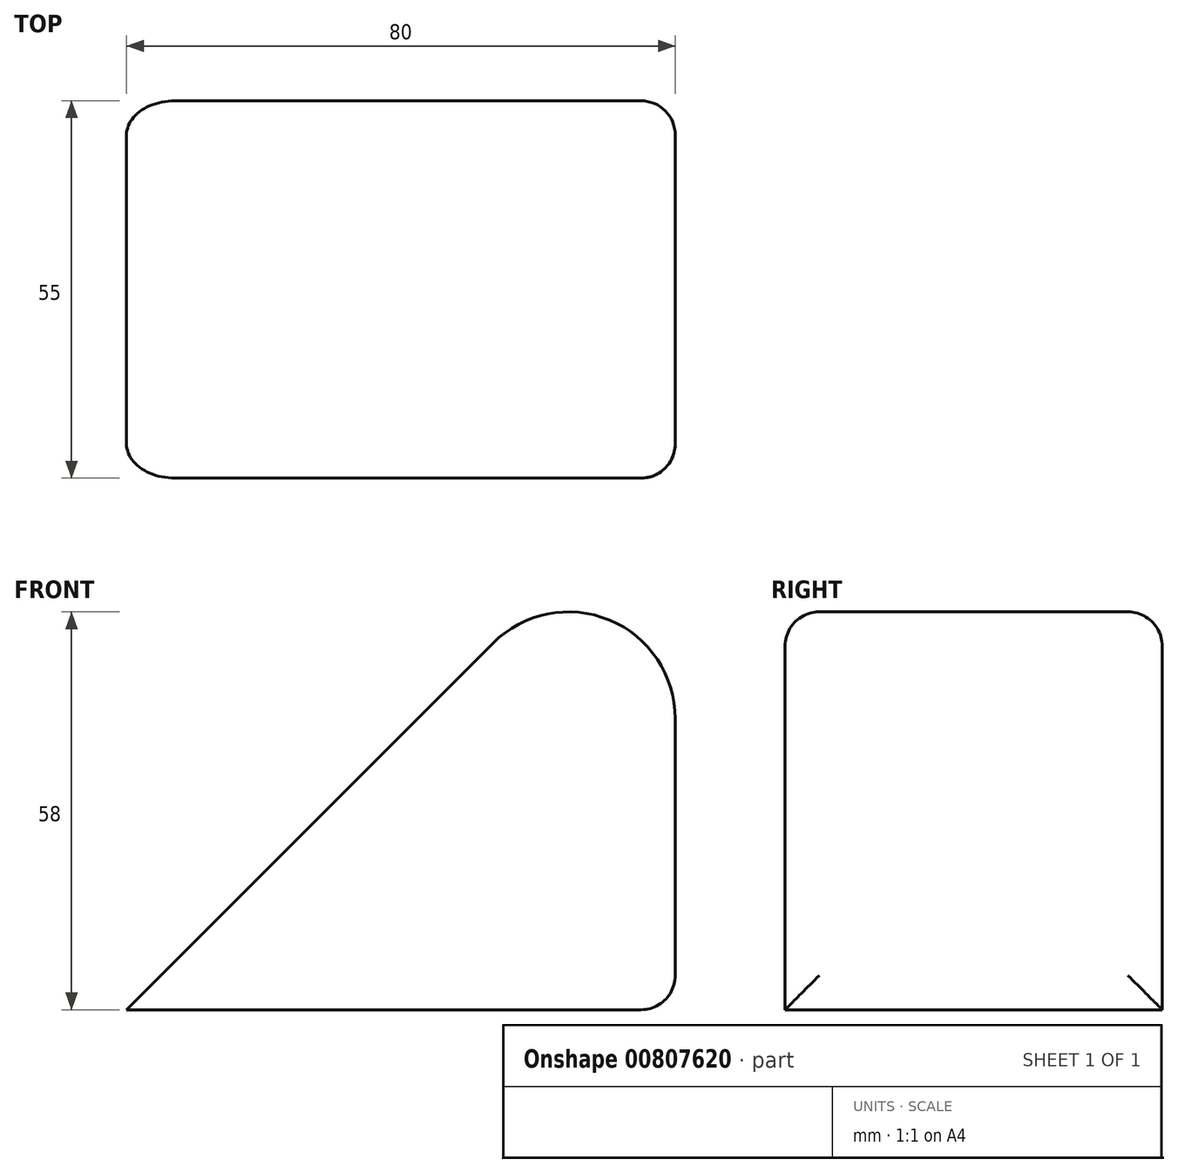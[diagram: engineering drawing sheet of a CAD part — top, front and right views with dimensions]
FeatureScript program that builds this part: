
annotation { "Feature Type Name" : "Feature", "Feature Type Description" : "" }
export const myFeature = defineFeature(function(context is Context, id is Id, definition is map)
    precondition{}
    {
        {
            var Q0;
            Q0=qCreatedBy(makeId("Front.planeOp"),FACE);
            var sketch = newSketch(context, id + "F0", { "sketchPlane" : qUnion([Q0])});
            skLineSegment(sketch, "E0", {"start": v(0, 0) * mm, "end": v(0, 80) * mm});
            skLineSegment(sketch, "E1", {"start": v(0, 80) * mm, "end": v(-80, 0) * mm});
            skLineSegment(sketch, "E2", {"start": v(-80, 0) * mm, "end": v(0, 0) * mm});
            skSolve(sketch);
        }
        {
            var Q0;
            Q0 = qSketchRegion(id + "F0", true);
            extrude(context, id + "F1", {"entities" : qUnion([Q0]), "depth" : 55 * mm, "offsetDistance" : 25 * mm});
        }
        {
            var Q0;
            Q0=makeQuery(id+"F1.opExtrude","SWEPT_EDGE",EDGE,{"disambiguationData":[OSD([sQuery(id+"F0.wireOp",EDGE,"E0"),sQuery(id+"F0.wireOp",EDGE,"E1")])]});
            fillet(context, id + "F2", {"entities" : qUnion([Q0]), "radius" : 15.56 * mm, "tangentPropagation" : true, "allowEdgeOverflow" : false});
        }
        {
            var Q0;
            Q0=makeQuery(id+"F1.opExtrude","CAP_EDGE",EDGE,{"disambiguationData":[OSD([sQuery(id+"F0.wireOp",EDGE,"E0")])],"isStart":false});
            var Q1;
            Q1=makeQuery(id+"F1.opExtrude","CAP_EDGE",EDGE,{"disambiguationData":[OSD([sQuery(id+"F0.wireOp",EDGE,"E0")])],"isStart":true});
            var Q2;
            Q2=makeQuery(id+"F1.opExtrude","SWEPT_EDGE",EDGE,{"disambiguationData":[OSD([sQuery(id+"F0.wireOp",EDGE,"E0"),sQuery(id+"F0.wireOp",EDGE,"E2")])]});
            fillet(context, id + "F3", {"entities" : qUnion([Q0, Q1, Q2]), "radius" : 5 * mm, "tangentPropagation" : true, "allowEdgeOverflow" : false});
        }
    });
